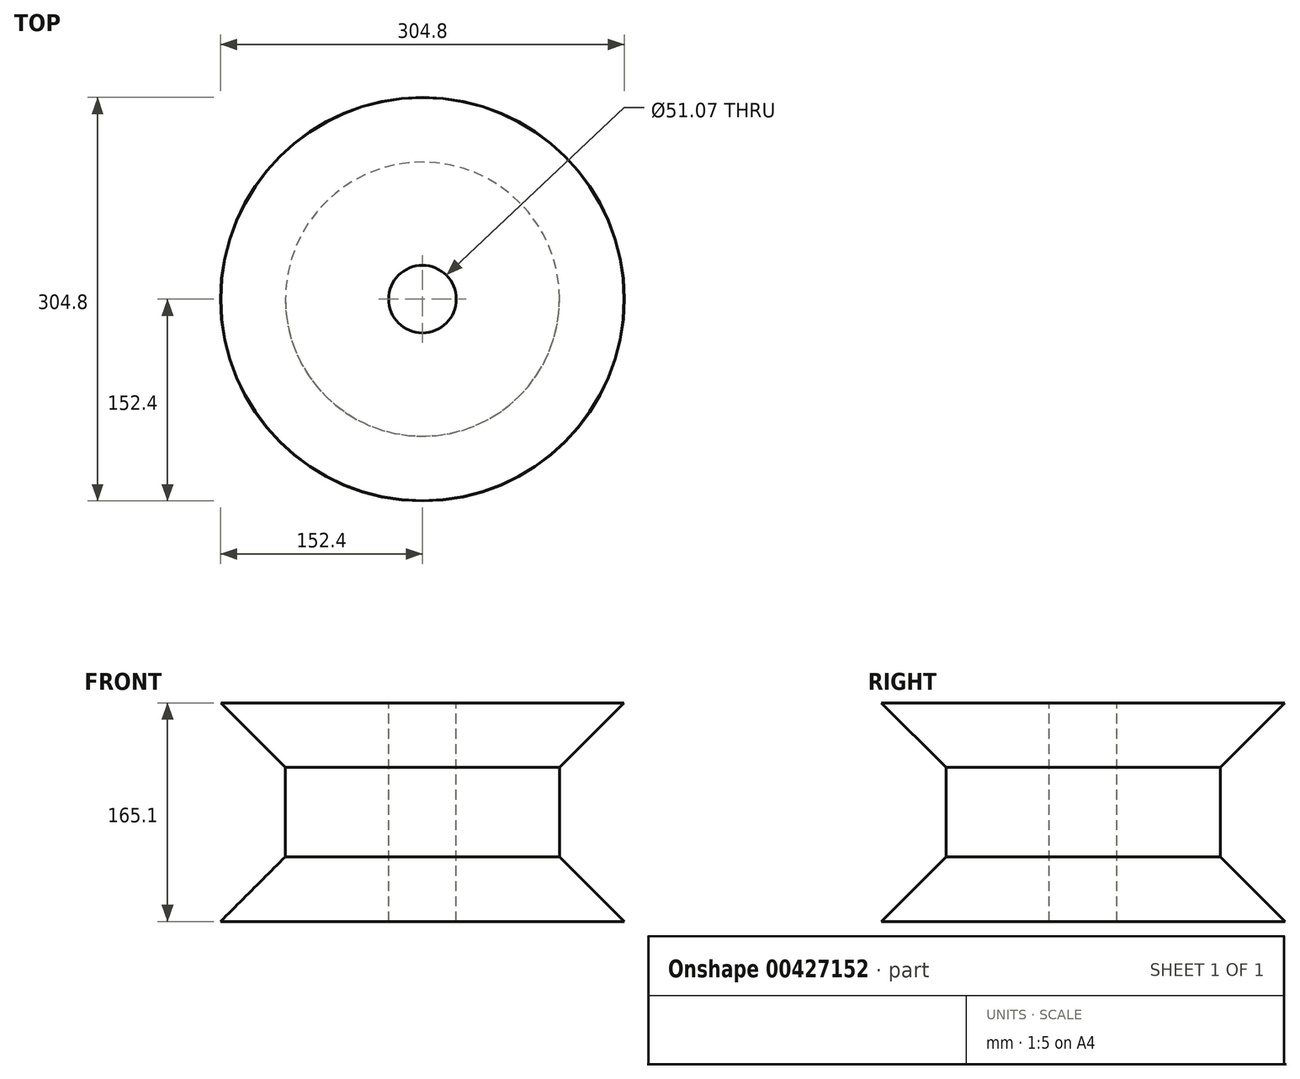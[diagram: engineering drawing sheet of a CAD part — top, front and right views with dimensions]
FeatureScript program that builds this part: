
annotation { "Feature Type Name" : "Feature", "Feature Type Description" : "" }
export const myFeature = defineFeature(function(context is Context, id is Id, definition is map)
    precondition{}
    {
        {
            var Q0;
            Q0=qCreatedBy(makeId("Top.planeOp"),FACE);
            var sketch = newSketch(context, id + "F0", { "sketchPlane" : qUnion([Q0])});
            skCircle(sketch, "E0", {"center": v(0, 0) * mm, "radius": 152.4 * mm});
            skSolve(sketch);
        }
        {
            var Q0;
            Q0 = qSketchRegion(id + "F0", true);
            extrude(context, id + "F1", {"entities" : qUnion([Q0]), "depth" : 50.8 * mm});
        }
        {
            var Q0;
            Q0=makeQuery(id+"F1.opExtrude","CAP_FACE",FACE,{"disambiguationData":[OSD([sQuery(id+"F0.wireOp",EDGE,"E0")])],"isStart":false});
            var sketch = newSketch(context, id + "F2", { "sketchPlane" : qUnion([Q0])});
            skCircle(sketch, "E1", {"center": v(0, 0) * mm, "radius": 103.48 * mm});
            skSolve(sketch);
        }
        {
            var Q0;
            Q0=makeQuery(id+"F2.imprint","IMPRINT",FACE,{"disambiguationData":[TD([[makeQuery(id+"F2.imprint","IMPRINT",EDGE,{"derivedFrom":sQuery(id+"F2.wireOp",EDGE,"E1")}),1.0]])]});
            extrude(context, id + "F3", {"entities" : qUnion([Q0]), "operationType" : NewBodyOperationType.ADD, "depth" : 63.5 * mm});
        }
        {
            var Q0;
            Q0=makeQuery(id+"F3.opExtrude","CAP_FACE",FACE,{"disambiguationData":[OSD([sQuery(id+"F2.wireOp",EDGE,"E1")])],"isStart":false});
            var sketch = newSketch(context, id + "F4", { "sketchPlane" : qUnion([Q0])});
            skSolve(sketch);
        }
        {
            var Q0;
            Q0=makeQuery(id+"F4.imprint","IMPRINT",FACE,{"disambiguationData":[TD([[makeQuery(id+"F4.imprint","IMPRINT",EDGE,{"derivedFrom":makeQuery(id+"F3.opExtrude","CAP_EDGE",EDGE,{"disambiguationData":[OSD([sQuery(id+"F2.wireOp",EDGE,"E1")])],"isStart":false})}),1.0]])]});
            var sketch = newSketch(context, id + "F5", { "sketchPlane" : qUnion([Q0])});
            skCircle(sketch, "E2", {"center": v(0, 0) * mm, "radius": 152.18 * mm});
            skSolve(sketch);
        }
        {
            var Q0;
            Q0 = qSketchRegion(id + "F5", true);
            extrude(context, id + "F6", {"entities" : qUnion([Q0]), "operationType" : NewBodyOperationType.ADD, "depth" : 50.8 * mm});
        }
        {
            var Q0;
            Q0=makeQuery(id+"F6.opExtrude","CAP_EDGE",EDGE,{"disambiguationData":[OSD([sQuery(id+"F5.wireOp",EDGE,"E2")])],"isStart":true});
            chamfer(context, id + "F7", {"entities" : qUnion([Q0]), "width" : 50.8 * mm, "tangentPropagation" : true});
        }
        {
            var Q0;
            Q0=makeQuery(id+"F1.opExtrude","CAP_EDGE",EDGE,{"disambiguationData":[OSD([sQuery(id+"F0.wireOp",EDGE,"E0")])],"isStart":false});
            chamfer(context, id + "F8", {"entities" : qUnion([Q0]), "width" : 50.8 * mm, "tangentPropagation" : true});
        }
        {
            var Q0;
            Q0=makeQuery(id+"F6.opExtrude","CAP_FACE",FACE,{"disambiguationData":[OSD([sQuery(id+"F5.wireOp",EDGE,"E2")])],"isStart":false});
            var sketch = newSketch(context, id + "F9", { "sketchPlane" : qUnion([Q0])});
            skCircle(sketch, "E3", {"center": v(0, 0) * mm, "radius": 25.54 * mm});
            skSolve(sketch);
        }
        {
            var Q0;
            Q0=makeQuery(id+"F9.imprint","IMPRINT",FACE,{"disambiguationData":[TD([[makeQuery(id+"F9.imprint","IMPRINT",EDGE,{"derivedFrom":sQuery(id+"F9.wireOp",EDGE,"E3")}),1.0]])]});
            extrude(context, id + "F10", {"entities" : qUnion([Q0]), "operationType" : NewBodyOperationType.REMOVE, "oppositeDirection" : true, "depth" : 203.2 * mm});
        }
    });
